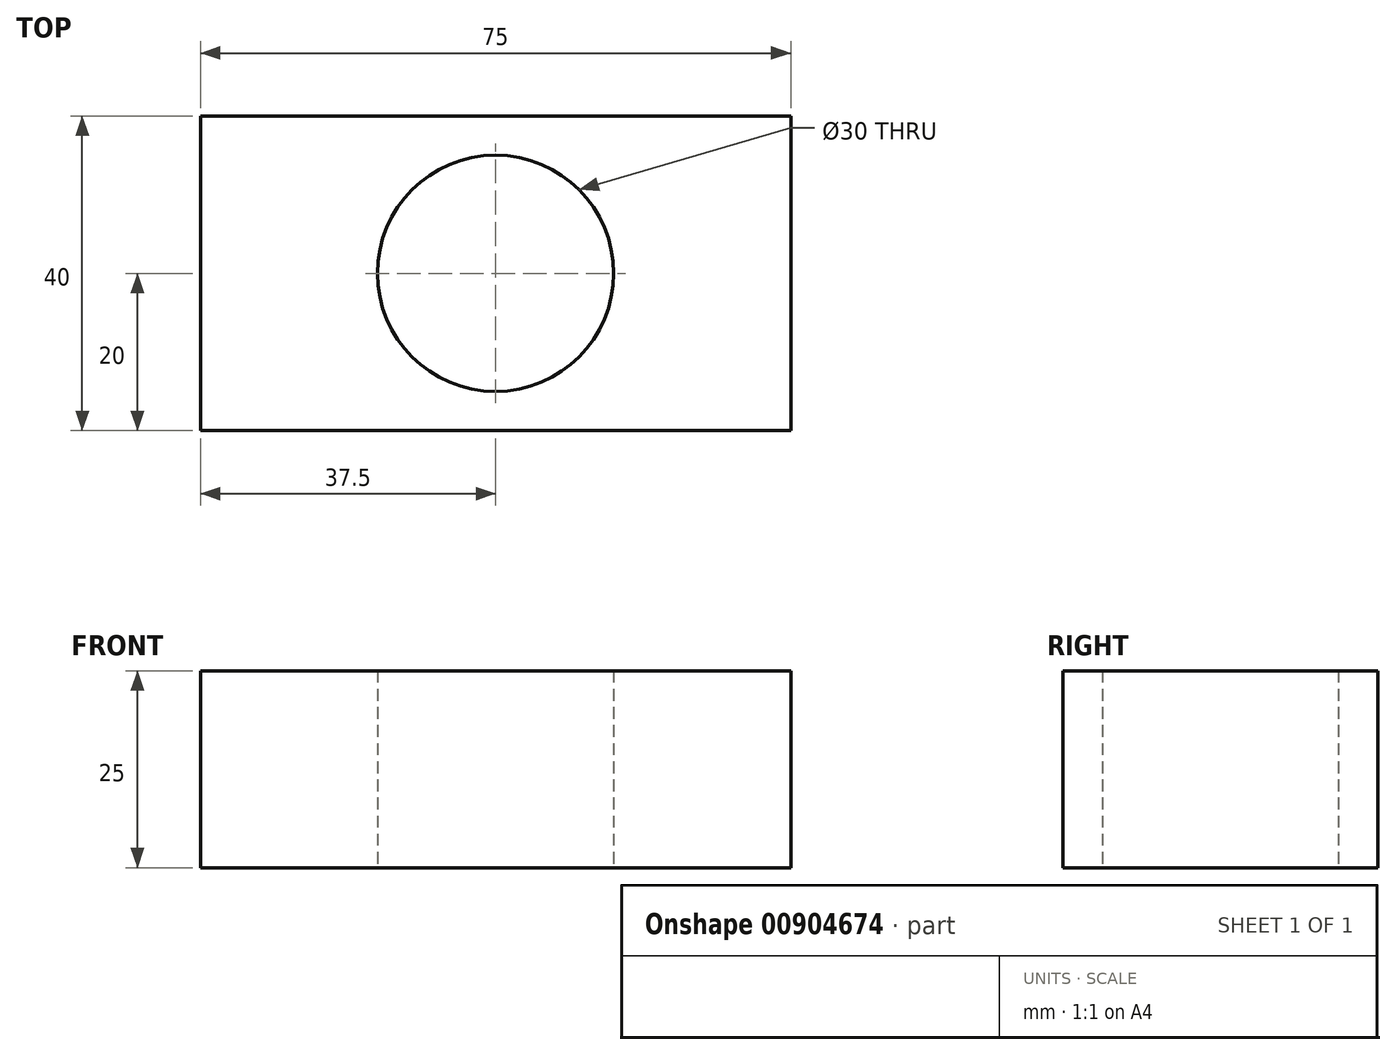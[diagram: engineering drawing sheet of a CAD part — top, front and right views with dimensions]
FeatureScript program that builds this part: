
annotation { "Feature Type Name" : "Feature", "Feature Type Description" : "" }
export const myFeature = defineFeature(function(context is Context, id is Id, definition is map)
    precondition{}
    {
        {
            var Q0;
            Q0=qCreatedBy(makeId("Top.planeOp"),FACE);
            var sketch = newSketch(context, id + "F0", { "sketchPlane" : qUnion([Q0])});
            skLineSegment(sketch, "E0.bottom", {"start": v(37.5, -20) * mm, "end": v(-37.5, -20) * mm});
            skLineSegment(sketch, "E0.top", {"start": v(37.5, 20) * mm, "end": v(-37.5, 20) * mm});
            skLineSegment(sketch, "E0.left", {"start": v(37.5, -20) * mm, "end": v(37.5, 20) * mm});
            skLineSegment(sketch, "E0.right", {"start": v(-37.5, -20) * mm, "end": v(-37.5, 20) * mm});
            skPoint(sketch, "E0.middle", {"position": v(0, 0) * mm});
            skCircle(sketch, "E1", {"center": v(0, 0) * mm, "radius": 15 * mm});
            skSolve(sketch);
        }
        {
            var Q0;
            Q0=makeQuery(id+"F0.imprint","IMPRINT",FACE,{"disambiguationData":[TD([[makeQuery(id+"F0.imprint","IMPRINT",EDGE,{"derivedFrom":sQuery(id+"F0.wireOp",EDGE,"E0.bottom")}),-1.0]])]});
            extrude(context, id + "F1", {"entities" : qUnion([Q0]), "depth" : 25 * mm, "offsetDistance" : 25 * mm});
        }
    });
